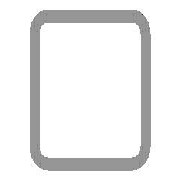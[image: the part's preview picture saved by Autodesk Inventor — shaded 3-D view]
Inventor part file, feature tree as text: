
AUTODESK INVENTOR PART (.ipt)
format: ipt  version: 2025 (Build 290162010, 162A)  size: 133,120 bytes
history: native  units: mm (DEFAULTED — no unit token found)
features: other x4, sketch x1, plane x1
ambient origin geometry x8: Origin, YZ Plane, XZ Plane, XY Plane, X Axis, Y Axis, Z Axis, Center Point
bodies: Solid1 (feature_tree), Body (feature_tree)
feature tree (6):
  parser-record x1  (decoder bookkeeping rows leaked as tree rows — omitted from the tree; the rows remain in map.json)
  other  "Driven Length"
  other  "Start Plane"
  other  "End Plane"
  sketch  "Sketch3"  dims[d3=3200.0mm d4=0.0mm d7=6.0mm d9=80.0mm d11=80.0mm d12=3.0mm d13=-0.0mm d14=3200.0mm d15=40.0mm d16=40.0mm d17=90.0deg d18=3200.0mm]
  plane  "Work Plane3"
